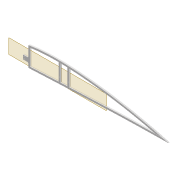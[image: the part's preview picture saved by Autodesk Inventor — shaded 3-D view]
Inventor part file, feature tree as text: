
AUTODESK INVENTOR PART (.ipt)
format: ipt  version: 2022 (Build 260153000, 153)  size: 414,208 bytes
history: native  units: mm
features: extrude x8, sketch x7, projected_geometry x6, fillet x2, shell x1, plane x1
ambient origin geometry x8: Origin, YZ Plane, XZ Plane, XY Plane, X Axis, Y Axis, Z Axis, Center Point
bodies: Solid1 (feature_tree)
feature tree (25):
  extrude  "Extrusion1"  Depth=5.0mm
  shell  "Shell1"  Thickness=2.0mm
  extrude  "Extrusion8"  Depth=5.9mm
  extrude  "Extrusion3"  Depth=10.0mm TaperAngle=0.0deg
  extrude  "Extrusion4"  Depth=2.0mm
  fillet  "Fillet1"  Radius=5.0mm
  sketch  "Sketch10"  dims[d22=4.0mm d23=0.0mm d31=2.0mm d32=5.0mm]
  extrude  "Extrusion5"  Depth=2.5mm
  plane  "Work Plane2"
  extrude  "Extrusion9"  Depth=1.6mm
  fillet  "Fillet2"  Radius=2.5mm
  extrude  "Extrusion10"  Depth=0.5mm
  extrude  "Extrusion11"  Depth=0.5mm TaperAngle=0.0deg
  sketch  "Sketch3"  dims[d0=4.0mm d1=0.0mm d2=5.0mm d7=2.0mm]
  sketch  "Sketch8"  dims[d8=2.0mm d9=5.9mm]
  sketch  "Sketch9"  dims[d13=10.0mm d14=0.0mm d16=10.0mm d17=0.0mm]
  projected_geometry  "Projected Loop4"
  projected_geometry  "Projected Loop10"
  sketch  "Sketch24"  dims[d34=1.6mm d35=2.5mm]
  projected_geometry  "Projected Loop11"
  projected_geometry  "Projected Loop12"
  projected_geometry  "Projected Loop13"
  sketch  "Sketch26"  dims[d37=5.0mm d38=1.6mm d40=2.5mm]
  projected_geometry  "Projected Loop14"
  sketch  "Sketch27"  dims[d62=80.0mm d63=6.0mm d64=4.0mm d65=0.0mm d66=3.0mm d67=12.0mm d68=5.0mm d69=15.0mm d70=12.0mm d71=3.05mm d72=10.0mm d73=0.0mm d74=2.0mm d75=100.0mm d76=20.0mm d77=0.5mm d78=10.0mm d79=0.0mm d80=10.0mm d81=0.0mm]
